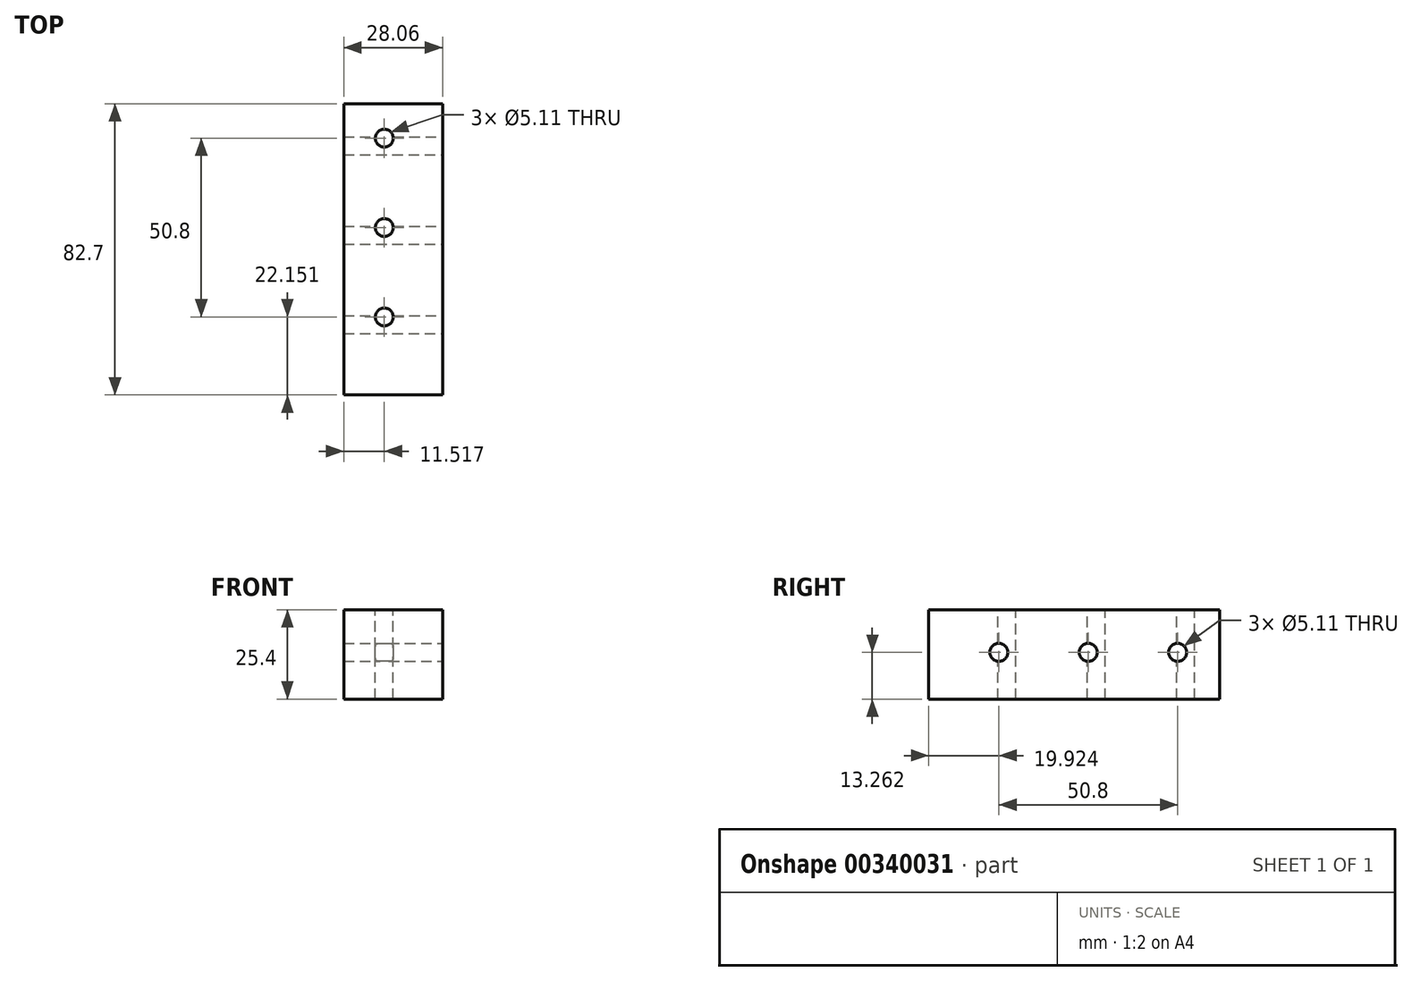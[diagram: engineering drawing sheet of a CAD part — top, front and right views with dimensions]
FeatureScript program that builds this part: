
annotation { "Feature Type Name" : "Feature", "Feature Type Description" : "" }
export const myFeature = defineFeature(function(context is Context, id is Id, definition is map)
    precondition{}
    {
        {
            var Q0;
            Q0=qCreatedBy(makeId("Top.planeOp"),FACE);
            var sketch = newSketch(context, id + "F0", { "sketchPlane" : qUnion([Q0])});
            skLineSegment(sketch, "E0.bottom", {"start": v(-33.56, 31.28) * mm, "end": v(-5.5, 31.28) * mm});
            skLineSegment(sketch, "E0.top", {"start": v(-33.56, -51.42) * mm, "end": v(-5.5, -51.42) * mm});
            skLineSegment(sketch, "E0.left", {"start": v(-33.56, 31.28) * mm, "end": v(-33.56, -51.42) * mm});
            skLineSegment(sketch, "E0.right", {"start": v(-5.5, 31.28) * mm, "end": v(-5.5, -51.42) * mm});
            skSolve(sketch);
        }
        {
            var Q0;
            Q0=makeQuery(id+"F0.imprint","IMPRINT",FACE,{"disambiguationData":[TD([[makeQuery(id+"F0.imprint","IMPRINT",EDGE,{"derivedFrom":sQuery(id+"F0.wireOp",EDGE,"E0.bottom")}),-1.0]])]});
            extrude(context, id + "F1", {"entities" : qUnion([Q0]), "depth" : 25.4 * mm});
        }
        {
            var Q0;
            Q0=makeQuery(id+"F1.opExtrude","CAP_FACE",FACE,{"disambiguationData":[OSD([sQuery(id+"F0.wireOp",EDGE,"E0.bottom"),sQuery(id+"F0.wireOp",EDGE,"E0.top"),sQuery(id+"F0.wireOp",EDGE,"E0.left"),sQuery(id+"F0.wireOp",EDGE,"E0.right")])],"isStart":false});
            var sketch = newSketch(context, id + "F2", { "sketchPlane" : qUnion([Q0])});
            skCircle(sketch, "E1", {"center": v(-22.04, 21.53) * mm, "radius": 4.61 * mm});
            skCircle(sketch, "E2.0.1.0", {"center": v(-22.04, -3.87) * mm, "radius": 4.61 * mm});
            skCircle(sketch, "E2.0.2.0", {"center": v(-22.04, -29.27) * mm, "radius": 4.61 * mm});
            skLineSegment(sketch, "E2.direction1", {"start": v(-22.04, 21.53) * mm, "end": v(3.36, 21.53) * mm, "construction": true});
            skLineSegment(sketch, "E2.direction2", {"start": v(-22.04, 21.53) * mm, "end": v(-22.04, -3.87) * mm, "construction": true});
            skSolve(sketch);
        }
        {
            var Q0;
            Q0=makeQuery(id+"F1.opExtrude","SWEPT_FACE",FACE,{"disambiguationData":[OSD([sQuery(id+"F0.wireOp",EDGE,"E0.right")])]});
            var sketch = newSketch(context, id + "F3", { "sketchPlane" : qUnion([Q0])});
            skCircle(sketch, "E3", {"center": v(19.3, 13.26) * mm, "radius": 6.34 * mm});
            skCircle(sketch, "E4.1.0.0", {"center": v(-6.1, 13.26) * mm, "radius": 6.34 * mm});
            skCircle(sketch, "E4.2.0.0", {"center": v(-31.5, 13.26) * mm, "radius": 6.34 * mm});
            skLineSegment(sketch, "E4.direction1", {"start": v(19.3, 13.26) * mm, "end": v(-6.1, 13.26) * mm, "construction": true});
            skSolve(sketch);
        }
        {
            var Q0;
            Q0=sQuery(id+"F3.wireOp",VERTEX,"E3.center");
            var Q1;
            Q1=sQuery(id+"F3.wireOp",VERTEX,"E4.1.0.0.center");
            var Q2;
            Q2=sQuery(id+"F3.wireOp",VERTEX,"E4.2.0.0.center");
            var Q3;
            Q3=makeQuery(id+"F1.opExtrude","SWEPT_BODY",BODY,{"disambiguationData":[OSD([sQuery(id+"F0.wireOp",EDGE,"E0.bottom"),sQuery(id+"F0.wireOp",EDGE,"E0.top"),sQuery(id+"F0.wireOp",EDGE,"E0.left"),sQuery(id+"F0.wireOp",EDGE,"E0.right")])]});
            hole(context, id + "F4", {"style" : HoleStyle.SIMPLE, "endStyle" : HoleEndStyle.THROUGH, "holeDiameter" : 5.1 * mm, "tappedDepth" : 12.7 * mm, "tapClearance" : 3, "locations" : qUnion([Q0, Q1, Q2]), "scope" : qUnion([Q3])});
        }
        {
            var Q0;
            Q0=sQuery(id+"F2.wireOp",VERTEX,"E1.center");
            var Q1;
            Q1=sQuery(id+"F2.wireOp",VERTEX,"E2.0.1.0.center");
            var Q2;
            Q2=sQuery(id+"F2.wireOp",VERTEX,"E2.0.2.0.center");
            var Q3;
            Q3=makeQuery(id+"F1.opExtrude","SWEPT_BODY",BODY,{"disambiguationData":[OSD([sQuery(id+"F0.wireOp",EDGE,"E0.bottom"),sQuery(id+"F0.wireOp",EDGE,"E0.top"),sQuery(id+"F0.wireOp",EDGE,"E0.left"),sQuery(id+"F0.wireOp",EDGE,"E0.right")])]});
            hole(context, id + "F5", {"style" : HoleStyle.SIMPLE, "endStyle" : HoleEndStyle.THROUGH, "holeDiameter" : 5.1 * mm, "tappedDepth" : 12.7 * mm, "tapClearance" : 3, "locations" : qUnion([Q0, Q1, Q2]), "scope" : qUnion([Q3])});
        }
    });
